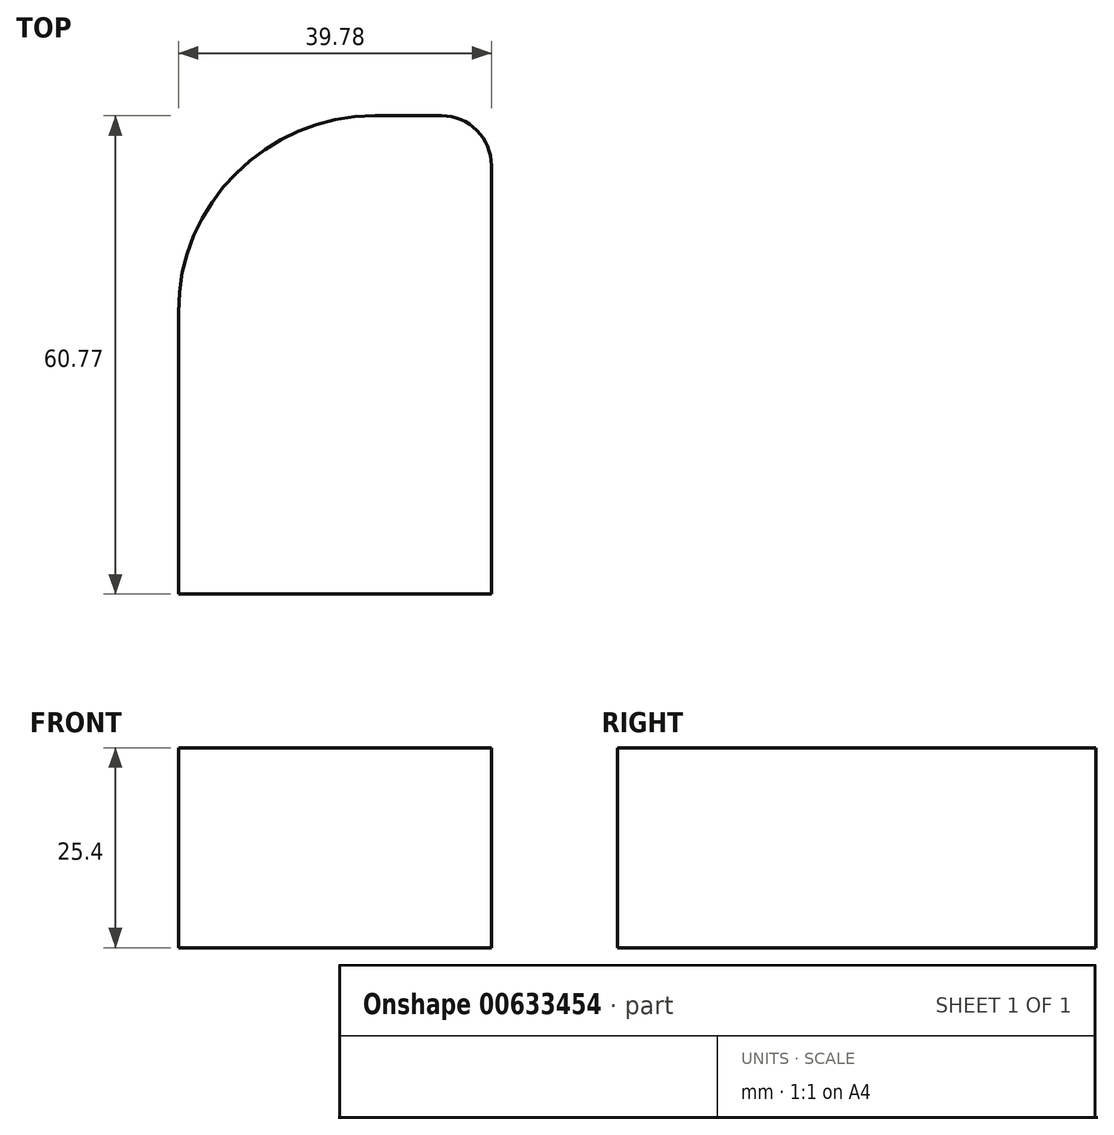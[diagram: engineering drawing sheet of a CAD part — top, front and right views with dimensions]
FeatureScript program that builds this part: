
annotation { "Feature Type Name" : "Feature", "Feature Type Description" : "" }
export const myFeature = defineFeature(function(context is Context, id is Id, definition is map)
    precondition{}
    {
        {
            var Q0;
            Q0=qCreatedBy(makeId("Top.planeOp"),FACE);
            var sketch = newSketch(context, id + "F0", { "sketchPlane" : qUnion([Q0])});
            skLineSegment(sketch, "E0.bottom", {"start": v(0, 0) * mm, "end": v(39.78, 0) * mm});
            skLineSegment(sketch, "E0.top", {"start": v(24.96, 60.77) * mm, "end": v(33.43, 60.77) * mm});
            skLineSegment(sketch, "E0.left", {"start": v(0, 0) * mm, "end": v(0, 35.81) * mm});
            skLineSegment(sketch, "E0.right", {"start": v(39.78, 0) * mm, "end": v(39.78, 54.42) * mm});
            skPoint(sketch, "E1.visualSharp", {"position": v(39.78, 60.77) * mm});
            skArc(sketch, "E1.filletArc", {"start": v(39.78, 54.42) * mm, "mid": v(37.92, 58.92) * mm, "end": v(33.43, 60.77) * mm});
            skPoint(sketch, "E2.visualSharp", {"position": v(0, 60.77) * mm});
            skArc(sketch, "E2.filletArc", {"start": v(24.96, 60.77) * mm, "mid": v(7.31, 53.46) * mm, "end": v(0, 35.81) * mm});
            skSolve(sketch);
        }
        {
            var Q0;
            Q0=makeQuery(id+"F0.imprint","IMPRINT",FACE,{"disambiguationData":[TD([[makeQuery(id+"F0.imprint","IMPRINT",EDGE,{"derivedFrom":sQuery(id+"F0.wireOp",EDGE,"E0.bottom")}),1.0]])]});
            extrude(context, id + "F1", {"entities" : qUnion([Q0]), "depth" : 25.4 * mm, "offsetDistance" : 25.4 * mm});
        }
    });
